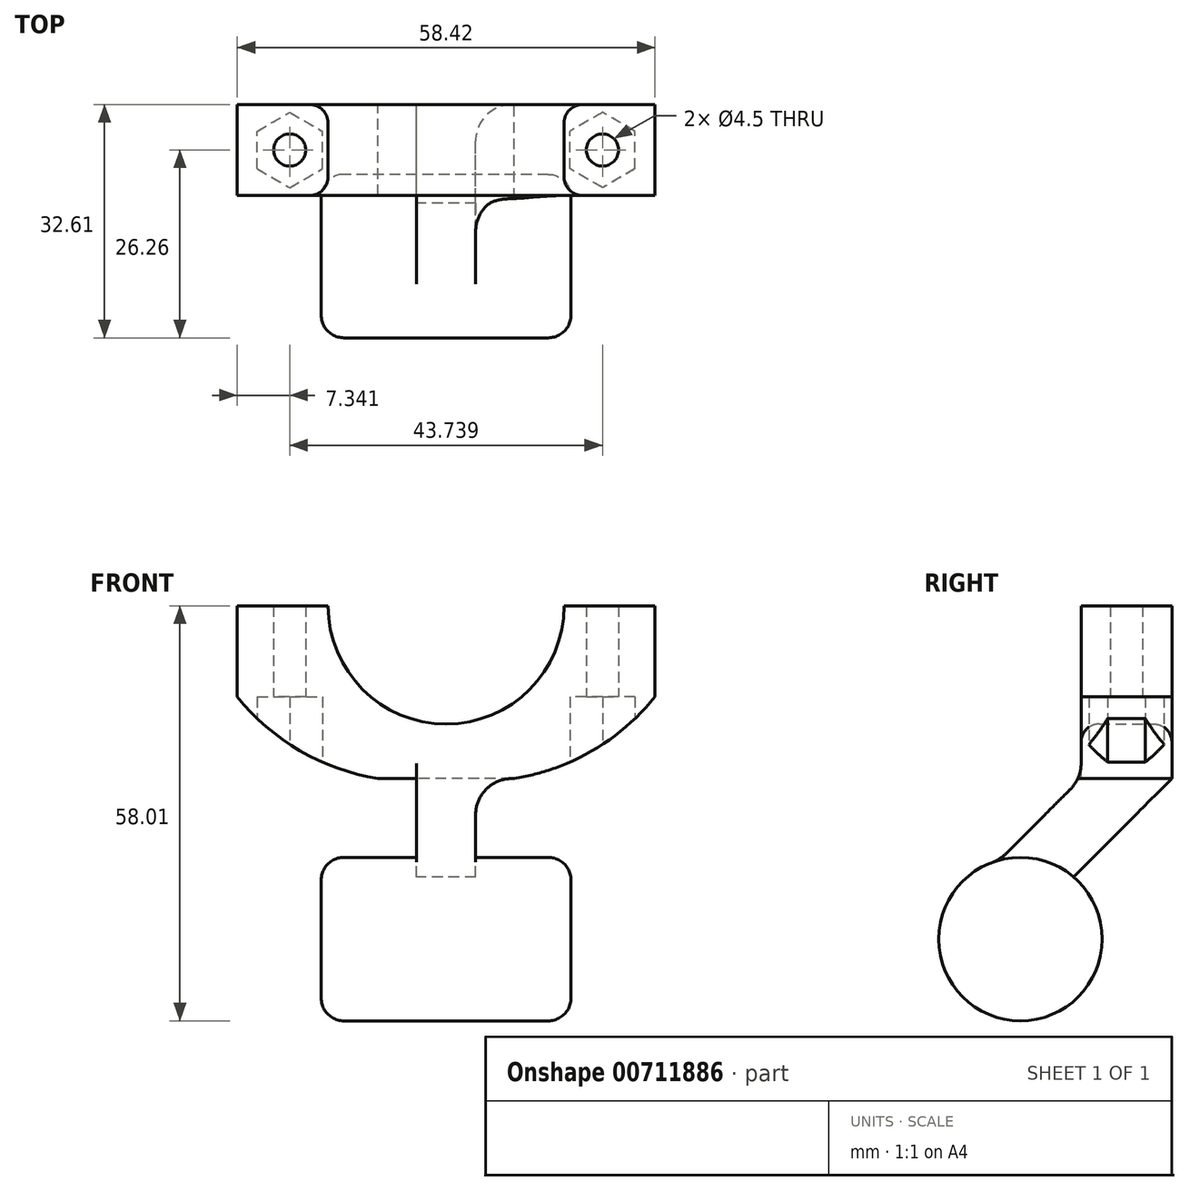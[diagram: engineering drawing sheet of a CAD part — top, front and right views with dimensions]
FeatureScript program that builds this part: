
annotation { "Feature Type Name" : "Feature", "Feature Type Description" : "" }
export const myFeature = defineFeature(function(context is Context, id is Id, definition is map)
    precondition{}
    {
        {
            var Q0;
            Q0=qCreatedBy(makeId("Front.planeOp"),FACE);
            var sketch = newSketch(context, id + "F0", { "sketchPlane" : qUnion([Q0])});
            skArc(sketch, "E0", {"start": v(0, -16.51) * mm, "mid": v(11.67, -11.67) * mm, "end": v(16.51, 0) * mm});
            skLineSegment(sketch, "E1", {"start": v(29.21, 0) * mm, "end": v(16.51, 0) * mm});
            skLineSegment(sketch, "E2", {"start": v(29.21, 0) * mm, "end": v(29.21, -24.13) * mm});
            skLineSegment(sketch, "E3", {"start": v(29.21, -24.13) * mm, "end": v(0, -24.13) * mm});
            skLineSegment(sketch, "E4", {"start": v(0, -24.13) * mm, "end": v(0, -16.51) * mm});
            skSolve(sketch);
        }
        {
            var Q0;
            Q0=makeQuery(id+"F0.imprint","IMPRINT",FACE,{"disambiguationData":[TD([[makeQuery(id+"F0.imprint","IMPRINT",EDGE,{"derivedFrom":sQuery(id+"F0.wireOp",EDGE,"E0")}),-1.0]])]});
            extrude(context, id + "F1", {"entities" : qUnion([Q0]), "endBound" : BoundingType.SYMMETRIC, "depth" : 50.8 * mm, "offsetDistance" : 25.4 * mm});
        }
        {
            var Q0;
            Q0=makeQuery(id+"F1.opExtrude","SWEPT_FACE",FACE,{"disambiguationData":[OSD([sQuery(id+"F0.wireOp",EDGE,"E3")])]});
            var sketch = newSketch(context, id + "F2", { "sketchPlane" : qUnion([Q0])});
            skPoint(sketch, "E5", {"position": v(21.87, -19.05) * mm});
            skPoint(sketch, "E6", {"position": v(21.87, 19.05) * mm});
            skLineSegment(sketch, "E7", {"start": v(21.87, -19.05) * mm, "end": v(21.87, -25.4) * mm});
            skLineSegment(sketch, "E8", {"start": v(21.87, 19.05) * mm, "end": v(21.87, 25.4) * mm});
            skSolve(sketch);
        }
        {
            var Q0;
            Q0=sQuery(id+"F2.wireOp",VERTEX,"E5");
            var Q1;
            Q1=sQuery(id+"F2.wireOp",VERTEX,"E6");
            var Q2;
            Q2=makeQuery(id+"F1.opExtrude","SWEPT_BODY",BODY,{"disambiguationData":[OSD([sQuery(id+"F0.wireOp",EDGE,"E0"),sQuery(id+"F0.wireOp",EDGE,"E1"),sQuery(id+"F0.wireOp",EDGE,"E2"),sQuery(id+"F0.wireOp",EDGE,"E3"),sQuery(id+"F0.wireOp",EDGE,"E4")])]});
            hole(context, id + "F3", {"style" : HoleStyle.SIMPLE, "endStyle" : HoleEndStyle.THROUGH, "standardTappedOrClearance" : lookupTablePath({ "standard" : "ANSI", "fit" : "Normal (ASME)", "size" : "#8", "type" : "Clearance" }), "standardBlindInLast" : lookupTablePath({ "fit" : "Free", "standard" : "ANSI", "size" : "#8", "type" : "Clearance" }), "holeDiameter" : 4.5 * mm, "majorDiameter" : 6.35 * mm, "isTappedThrough" : true, "tappedDepth" : 12.7 * mm, "tapClearance" : 3, "startFromSketch" : true, "locations" : qUnion([Q0, Q1]), "scope" : qUnion([Q2])});
        }
        {
            var Q0;
            Q0=makeQuery(id+"F1.opExtrude","SWEPT_FACE",FACE,{"disambiguationData":[OSD([sQuery(id+"F0.wireOp",EDGE,"E3")])]});
            var sketch = newSketch(context, id + "F4", { "sketchPlane" : qUnion([Q0])});
            skCircle(sketch, "E9.cCircle", {"center": v(21.87, -19.05) * mm, "radius": 4.56 * mm, "construction": true});
            skLineSegment(sketch, "E9.0", {"start": v(17.31, -21.68) * mm, "end": v(17.31, -16.42) * mm});
            skLineSegment(sketch, "E9.1", {"start": v(17.31, -16.42) * mm, "end": v(21.87, -13.79) * mm});
            skLineSegment(sketch, "E9.2", {"start": v(21.87, -13.79) * mm, "end": v(26.43, -16.42) * mm});
            skLineSegment(sketch, "E9.3", {"start": v(26.43, -16.42) * mm, "end": v(26.43, -21.68) * mm});
            skLineSegment(sketch, "E9.4", {"start": v(26.43, -21.68) * mm, "end": v(21.87, -24.31) * mm});
            skLineSegment(sketch, "E9.5", {"start": v(21.87, -24.31) * mm, "end": v(17.31, -21.68) * mm});
            skPoint(sketch, "E9.0.midPoint", {"position": v(17.31, -19.05) * mm});
            skCircle(sketch, "E10.cCircle", {"center": v(21.87, 19.05) * mm, "radius": 4.56 * mm, "construction": true});
            skPoint(sketch, "E10.cCircle.perimeterSnap0", {"position": v(19.59, -15.1) * mm});
            skLineSegment(sketch, "E10.0", {"start": v(21.87, 13.79) * mm, "end": v(17.31, 16.42) * mm});
            skLineSegment(sketch, "E10.1", {"start": v(17.31, 16.42) * mm, "end": v(17.31, 21.68) * mm});
            skLineSegment(sketch, "E10.2", {"start": v(17.31, 21.68) * mm, "end": v(21.87, 24.31) * mm});
            skLineSegment(sketch, "E10.3", {"start": v(21.87, 24.31) * mm, "end": v(26.43, 21.68) * mm});
            skLineSegment(sketch, "E10.4", {"start": v(26.43, 21.68) * mm, "end": v(26.43, 16.42) * mm});
            skLineSegment(sketch, "E10.5", {"start": v(26.43, 16.42) * mm, "end": v(21.87, 13.79) * mm});
            skPoint(sketch, "E10.0.midPoint", {"position": v(19.59, 15.1) * mm});
            skPoint(sketch, "E10.0.midPoint.positionSnap0", {"position": v(19.59, -15.1) * mm});
            skSolve(sketch);
        }
        {
            var Q0;
            Q0=makeQuery(id+"F1.opExtrude","CAP_FACE",FACE,{"disambiguationData":[OSD([sQuery(id+"F0.wireOp",EDGE,"E0"),sQuery(id+"F0.wireOp",EDGE,"E1"),sQuery(id+"F0.wireOp",EDGE,"E2"),sQuery(id+"F0.wireOp",EDGE,"E3"),sQuery(id+"F0.wireOp",EDGE,"E4")])],"isStart":true});
            var sketch = newSketch(context, id + "F5", { "sketchPlane" : qUnion([Q0])});
            skLineSegment(sketch, "E11", {"start": v(-9.53, -24.13) * mm, "end": v(-29.21, -24.13) * mm});
            skLineSegment(sketch, "E12", {"start": v(-29.21, -24.13) * mm, "end": v(-29.21, -12.7) * mm});
            skArc(sketch, "E13", {"start": v(-29.21, -12.7) * mm, "mid": v(-20.43, -20.24) * mm, "end": v(-9.53, -24.13) * mm});
            skSolve(sketch);
        }
        {
            var Q0;
            Q0=makeQuery(id+"F5.imprint","IMPRINT",FACE,{"disambiguationData":[TD([[makeQuery(id+"F5.imprint","IMPRINT",EDGE,{"derivedFrom":sQuery(id+"F5.wireOp",EDGE,"E11")}),1.0]])]});
            extrude(context, id + "F6", {"entities" : qUnion([Q0]), "operationType" : NewBodyOperationType.REMOVE, "endBound" : BoundingType.THROUGH_ALL, "oppositeDirection" : true, "depth" : 25.4 * mm, "offsetDistance" : 25.4 * mm});
        }
        {
            var Q0;
            Q0 = qSketchRegion(id + "F4", true);
            var Q1;
            Q1=makeQuery(id+"F1.opExtrude","SWEPT_FACE",FACE,{"disambiguationData":[OSD([sQuery(id+"F0.wireOp",EDGE,"E1")])]});
            extrude(context, id + "F7", {"entities" : qUnion([Q0]), "operationType" : NewBodyOperationType.REMOVE, "endBound" : BoundingType.UP_TO_SURFACE, "oppositeDirection" : true, "depth" : 25.4 * mm, "endBoundEntityFace" : qUnion([Q1]), "hasOffset" : true, "offsetDistance" : 12.7 * mm});
        }
        {
            var Q0;
            Q0=makeQuery(id+"F1.opExtrude","SWEPT_BODY",BODY,{"disambiguationData":[OSD([sQuery(id+"F0.wireOp",EDGE,"E0"),sQuery(id+"F0.wireOp",EDGE,"E1"),sQuery(id+"F0.wireOp",EDGE,"E2"),sQuery(id+"F0.wireOp",EDGE,"E3"),sQuery(id+"F0.wireOp",EDGE,"E4")])]});
            var Q1;
            Q1=qCreatedBy(makeId("Right.planeOp"),FACE);
            mirror(context, id + "F8", {"operationType" : NewBodyOperationType.ADD, "entities" : qUnion([Q0]), "mirrorPlane" : qUnion([Q1])});
        }
        {
            var Q0;
            {var subQ0=makeQuery(id+"F1.opExtrude","CAP_EDGE",EDGE,{"disambiguationData":[OSD([sQuery(id+"F0.wireOp",EDGE,"E0")])],"isStart":true});Q0=makeQuery(id+"F8.boolean.opBoolean","MERGE",EDGE,{"derivedFrom":[subQ0,makeQuery(id+"F8.opPattern","COPY",EDGE,{"derivedFrom":subQ0,"instanceName":"1"})]});}
            var Q1;
            {var subQ0=makeQuery(id+"F1.opExtrude","CAP_EDGE",EDGE,{"disambiguationData":[OSD([sQuery(id+"F0.wireOp",EDGE,"E0")])],"isStart":false});Q1=makeQuery(id+"F8.boolean.opBoolean","MERGE",EDGE,{"derivedFrom":[subQ0,makeQuery(id+"F8.opPattern","COPY",EDGE,{"derivedFrom":subQ0,"instanceName":"1"})]});}
            fillet(context, id + "F9", {"entities" : qUnion([Q0, Q1]), "radius" : 2.54 * mm, "tangentPropagation" : true, "allowEdgeOverflow" : false});
        }
        {
            var Q0;
            Q0=makeQuery(id+"F1.opExtrude","SWEPT_FACE",FACE,{"disambiguationData":[OSD([sQuery(id+"F0.wireOp",EDGE,"E1")])]});
            var sketch = newSketch(context, id + "F10", { "sketchPlane" : qUnion([Q0])});
            skLineSegment(sketch, "E14", {"start": v(-29.21, -19.05) * mm, "end": v(29.21, -19.05) * mm});
            skPoint(sketch, "E15", {"position": v(21.87, -19.05) * mm});
            skLineSegment(sketch, "E16", {"start": v(29.21, 25.4) * mm, "end": v(29.21, -19.05) * mm});
            skLineSegment(sketch, "E17", {"start": v(29.21, 25.4) * mm, "end": v(-29.21, 25.4) * mm});
            skLineSegment(sketch, "E18", {"start": v(-29.21, 25.4) * mm, "end": v(-29.21, -19.05) * mm});
            skSolve(sketch);
        }
        {
            var Q0;
            Q0 = qSketchRegion(id + "F10", true);
            extrude(context, id + "F11", {"entities" : qUnion([Q0]), "operationType" : NewBodyOperationType.REMOVE, "endBound" : BoundingType.THROUGH_ALL, "oppositeDirection" : true, "depth" : 25.4 * mm, "offsetDistance" : 25.4 * mm});
        }
        {
            var Q0;
            Q0=makeQuery(id+"F1.opExtrude","SWEPT_BODY",BODY,{"disambiguationData":[OSD([sQuery(id+"F0.wireOp",EDGE,"E0"),sQuery(id+"F0.wireOp",EDGE,"E1"),sQuery(id+"F0.wireOp",EDGE,"E2"),sQuery(id+"F0.wireOp",EDGE,"E3"),sQuery(id+"F0.wireOp",EDGE,"E4")])]});
            var Q1;
            {var subQ2=makeQuery(id+"F1.opExtrude","SWEPT_FACE",FACE,{"disambiguationData":[OSD([sQuery(id+"F0.wireOp",EDGE,"E0")])]});Q1=makeQuery(id+"F11.boolean.opBoolean","COPY",FACE,{"disambiguationData":[TD([subQ2])],"derivedFrom":makeQuery(id+"F11.opExtrude","SWEPT_FACE",FACE,{"disambiguationData":[OSD([sQuery(id+"F10.wireOp",EDGE,"E14")])]})});}
            mirror(context, id + "F12", {"operationType" : NewBodyOperationType.ADD, "entities" : qUnion([Q0]), "mirrorPlane" : qUnion([Q1])});
        }
        {
            var Q0;
            {var subQ0=makeQuery(id+"F1.opExtrude","CAP_FACE",FACE,{"disambiguationData":[OSD([sQuery(id+"F0.wireOp",EDGE,"E0"),sQuery(id+"F0.wireOp",EDGE,"E1"),sQuery(id+"F0.wireOp",EDGE,"E2"),sQuery(id+"F0.wireOp",EDGE,"E3"),sQuery(id+"F0.wireOp",EDGE,"E4")])],"isStart":false});Q0=makeQuery(id+"F12.opPattern","COPY",FACE,{"derivedFrom":makeQuery(id+"F8.boolean.opBoolean","MERGE",FACE,{"derivedFrom":[subQ0,makeQuery(id+"F8.opPattern","COPY",FACE,{"derivedFrom":subQ0,"instanceName":"1"})]}),"instanceName":"1"});}
            var sketch = newSketch(context, id + "F13", { "sketchPlane" : qUnion([Q0])});
            skArc(sketch, "E19", {"start": v(-8.49, -39.18) * mm, "mid": v(0, -59.06) * mm, "end": v(8.49, -39.18) * mm});
            skPoint(sketch, "E20", {"position": v(0, -35.56) * mm});
            skPoint(sketch, "E21", {"position": v(0, -16.51) * mm});
            skArc(sketch, "E22", {"start": v(-8.49, -39.18) * mm, "mid": v(-6.19, -30.05) * mm, "end": v(-12.86, -23.4) * mm});
            skArc(sketch, "E23", {"start": v(12.86, -23.4) * mm, "mid": v(6.19, -30.05) * mm, "end": v(8.49, -39.18) * mm});
            skLineSegment(sketch, "E24", {"start": v(-12.86, -23.4) * mm, "end": v(12.86, -23.4) * mm});
            skPoint(sketch, "E25", {"position": v(-12.86, -23.4) * mm});
            skSolve(sketch);
        }
        {
            var Q0;
            Q0=qCreatedBy(makeId("Right.planeOp"),FACE);
            var sketch = newSketch(context, id + "F14", { "sketchPlane" : qUnion([Q0])});
            skLineSegment(sketch, "E26", {"start": v(-43.51, -42.24) * mm, "end": v(-25.4, -24.13) * mm});
            skLineSegment(sketch, "E27", {"start": v(-35.15, -46.58) * mm, "end": v(-12.7, -24.13) * mm});
            skLineSegment(sketch, "E28", {"start": v(-35.15, -46.58) * mm, "end": v(-41.72, -46.58) * mm});
            skLineSegment(sketch, "E29", {"start": v(-25.4, -24.13) * mm, "end": v(-12.7, -24.13) * mm});
            skPoint(sketch, "E30.visualSharp", {"position": v(-47.85, -46.58) * mm});
            skArc(sketch, "E30.filletArc", {"start": v(-43.51, -42.24) * mm, "mid": v(-44.07, -45.01) * mm, "end": v(-41.72, -46.58) * mm});
            skSolve(sketch);
        }
        {
            var Q0;
            Q0 = qSketchRegion(id + "F14", true);
            extrude(context, id + "F15", {"entities" : qUnion([Q0]), "operationType" : NewBodyOperationType.ADD, "endBound" : BoundingType.SYMMETRIC, "depth" : 8.25 * mm, "offsetDistance" : 25.4 * mm});
        }
        {
            var Q0;
            Q0=qCreatedBy(makeId("Right.planeOp"),FACE);
            var sketch = newSketch(context, id + "F16", { "sketchPlane" : qUnion([Q0])});
            skCircle(sketch, "E31", {"center": v(-33.88, -46.58) * mm, "radius": 11.43 * mm});
            skSolve(sketch);
        }
        {
            var Q0;
            Q0=makeQuery(id+"F16.imprint","IMPRINT",FACE,{"disambiguationData":[TD([[makeQuery(id+"F16.imprint","IMPRINT",EDGE,{"derivedFrom":sQuery(id+"F16.wireOp",EDGE,"E31")}),1.0]])]});
            extrude(context, id + "F17", {"entities" : qUnion([Q0]), "operationType" : NewBodyOperationType.ADD, "endBound" : BoundingType.SYMMETRIC, "depth" : 34.92 * mm, "offsetDistance" : 25.4 * mm});
        }
        {
            var Q0;
            Q0=makeQuery(id+"F15.opExtrude","CAP_EDGE",EDGE,{"disambiguationData":[OSD([sQuery(id+"F14.wireOp",EDGE,"E29")])],"isStart":true});
            var Q1;
            Q1=makeQuery(id+"F15.opExtrude","CAP_EDGE",EDGE,{"disambiguationData":[OSD([sQuery(id+"F14.wireOp",EDGE,"E29")])],"isStart":false});
            var Q2;
            {var subQ0=makeQuery(id+"F1.opExtrude","CAP_EDGE",EDGE,{"disambiguationData":[OSD([sQuery(id+"F0.wireOp",EDGE,"E3")])],"isStart":false});Q2=makeQuery(id+"F15.boolean.opBoolean","MERGE",EDGE,{"derivedFrom":[makeQuery(id+"F8.boolean.opBoolean","MERGE",EDGE,{"derivedFrom":[subQ0,makeQuery(id+"F8.opPattern","COPY",EDGE,{"derivedFrom":subQ0,"instanceName":"1"})]}),makeQuery(id+"F15.opExtrude","SWEPT_EDGE",EDGE,{"disambiguationData":[OSD([sQuery(id+"F14.wireOp",EDGE,"E26"),sQuery(id+"F14.wireOp",EDGE,"E29")])]})]});}
            var Q3;
            Q3=makeQuery(id+"F17.boolean.opBoolean","INTERSECT",EDGE,{"derivedFrom":[makeQuery(id+"F15.opExtrude","SWEPT_FACE",FACE,{"disambiguationData":[OSD([sQuery(id+"F14.wireOp",EDGE,"E26")])]}),makeQuery(id+"F17.opExtrude","SWEPT_FACE",FACE,{"disambiguationData":[OSD([sQuery(id+"F16.wireOp",EDGE,"E31")])]})]});
            fillet(context, id + "F18", {"entities" : qUnion([Q0, Q1, Q2, Q3]), "tangentPropagation" : true, "radius" : 5.08 * mm, "defaultsChanged" : false, "vertexSettings" : [], "allowEdgeOverflow" : false});
        }
        {
            var Q0;
            Q0=makeQuery(id+"F17.opExtrude","CAP_EDGE",EDGE,{"disambiguationData":[OSD([sQuery(id+"F16.wireOp",EDGE,"E31")])],"isStart":true});
            var Q1;
            Q1=makeQuery(id+"F17.opExtrude","CAP_EDGE",EDGE,{"disambiguationData":[OSD([sQuery(id+"F16.wireOp",EDGE,"E31")])],"isStart":false});
            fillet(context, id + "F19", {"entities" : qUnion([Q0, Q1]), "tangentPropagation" : true, "radius" : 3.17 * mm, "defaultsChanged" : true, "vertexSettings" : [], "allowEdgeOverflow" : false});
        }
    });
